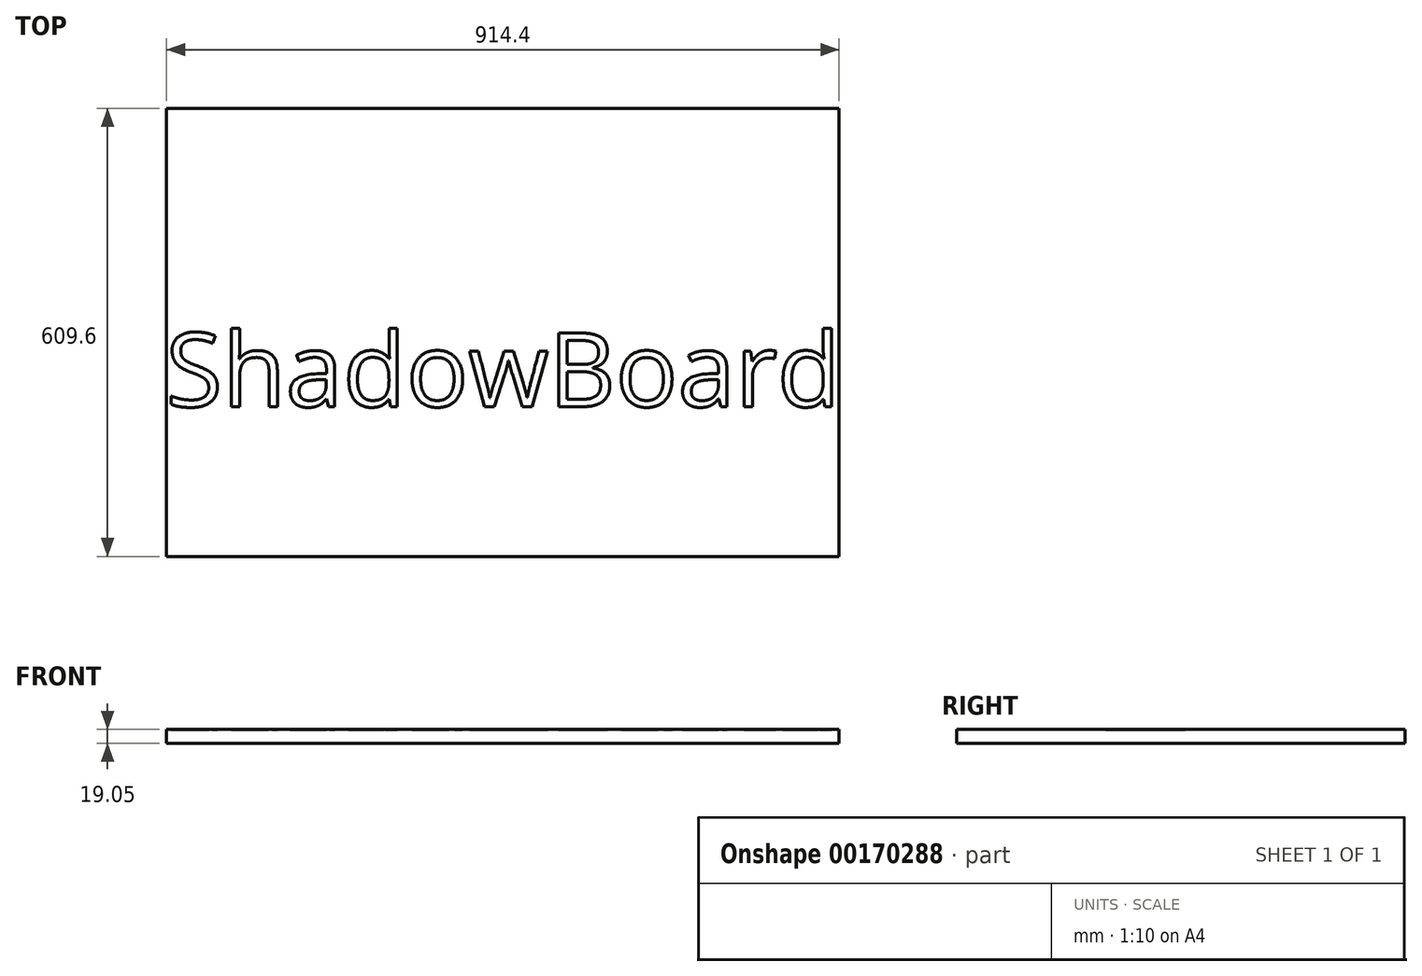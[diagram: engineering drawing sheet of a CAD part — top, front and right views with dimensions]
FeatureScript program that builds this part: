
annotation { "Feature Type Name" : "Feature", "Feature Type Description" : "" }
export const myFeature = defineFeature(function(context is Context, id is Id, definition is map)
    precondition{}
    {
        {
            var Q0;
            Q0=qCreatedBy(makeId("Top.planeOp"),FACE);
            var sketch = newSketch(context, id + "F0", { "sketchPlane" : qUnion([Q0])});
            skLineSegment(sketch, "E0.bottom", {"start": v(457.2, 304.8) * mm, "end": v(-457.2, 304.8) * mm});
            skLineSegment(sketch, "E0.top", {"start": v(457.2, -304.8) * mm, "end": v(-457.2, -304.8) * mm});
            skLineSegment(sketch, "E0.left", {"start": v(457.2, 304.8) * mm, "end": v(457.2, -304.8) * mm});
            skLineSegment(sketch, "E0.right", {"start": v(-457.2, 304.8) * mm, "end": v(-457.2, -304.8) * mm});
            skPoint(sketch, "E0.middle", {"position": v(0, 0) * mm});
            skSolve(sketch);
        }
        {
            var Q0;
            Q0 = qSketchRegion(id + "F0", true);
            extrude(context, id + "F1", {"entities" : qUnion([Q0]), "depth" : 19.05 * mm});
        }
        {
            var Q0;
            Q0=makeQuery(id+"F1.opExtrude","CAP_FACE",FACE,{"disambiguationData":[OSD([sQuery(id+"F0.wireOp",EDGE,"E0.bottom"),sQuery(id+"F0.wireOp",EDGE,"E0.top"),sQuery(id+"F0.wireOp",EDGE,"E0.left"),sQuery(id+"F0.wireOp",EDGE,"E0.right")])],"isStart":false});
            var sketch = newSketch(context, id + "F2", { "sketchPlane" : qUnion([Q0])});
            skText(sketch, "E1", { "text": "ShadowBoard", "fontName": "OpenSans-Regular.ttf"});
            const initialGuessF2  = {"E1": [-0.45827, -0.1008, 1, 0, 0.10095]};
            skSetInitialGuess(sketch, initialGuessF2);
            skSolve(sketch);
        }
        {
            var Q0;
            Q0 = qSketchRegion(id + "F2", true);
            extrude(context, id + "F3", {"entities" : qUnion([Q0]), "operationType" : NewBodyOperationType.REMOVE, "oppositeDirection" : true, "depth" : 1.59 * mm});
        }
    });
